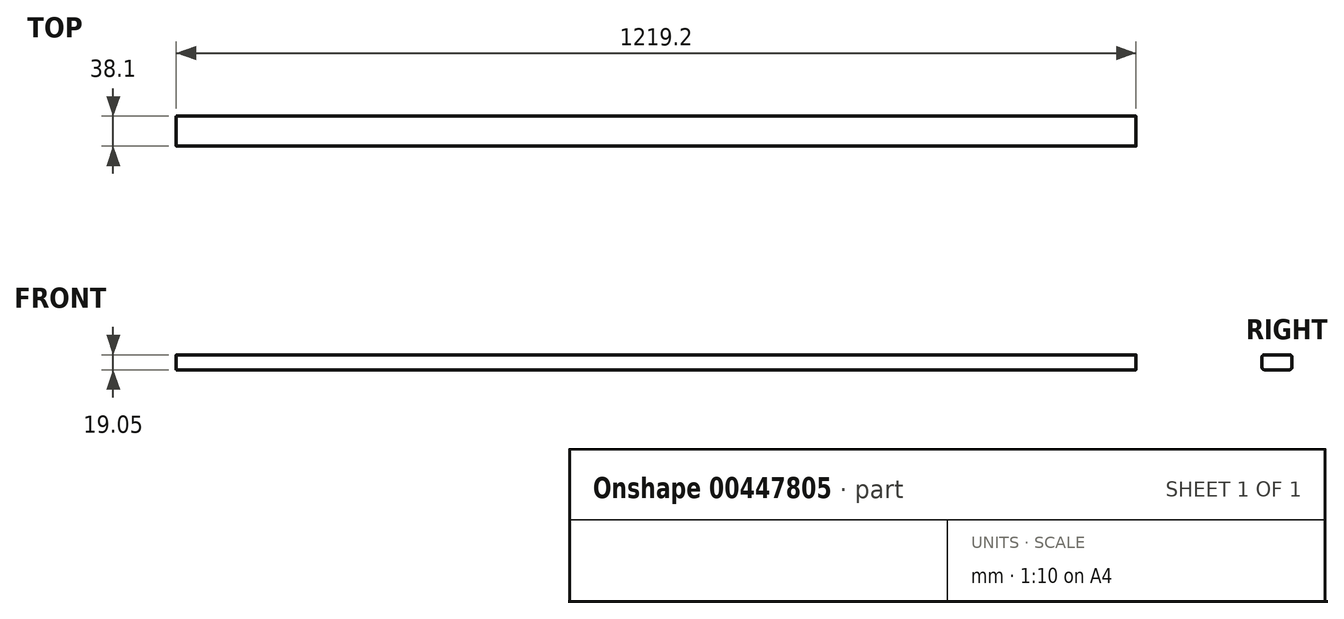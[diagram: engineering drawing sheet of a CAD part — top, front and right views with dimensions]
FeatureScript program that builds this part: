
annotation { "Feature Type Name" : "Feature", "Feature Type Description" : "" }
export const myFeature = defineFeature(function(context is Context, id is Id, definition is map)
    precondition{}
    {
        {
            var Q0;
            Q0=qCreatedBy(makeId("Right.planeOp"),FACE);
            var sketch = newSketch(context, id + "F0", { "sketchPlane" : qUnion([Q0])});
            skLineSegment(sketch, "E0.bottom", {"start": v(3.17, 0) * mm, "end": v(34.93, 0) * mm});
            skLineSegment(sketch, "E0.top", {"start": v(3.17, 19.05) * mm, "end": v(34.93, 19.05) * mm});
            skLineSegment(sketch, "E0.left", {"start": v(0, 3.18) * mm, "end": v(0, 15.88) * mm});
            skLineSegment(sketch, "E0.right", {"start": v(38.1, 3.18) * mm, "end": v(38.1, 15.88) * mm});
            skPoint(sketch, "E1.visualSharp", {"position": v(0, 19.05) * mm});
            skArc(sketch, "E1.filletArc", {"start": v(3.17, 19.05) * mm, "mid": v(0.93, 18.12) * mm, "end": v(0, 15.88) * mm});
            skPoint(sketch, "E2.visualSharp", {"position": v(0, 0) * mm});
            skArc(sketch, "E2.filletArc", {"start": v(0, 3.17) * mm, "mid": v(0.93, 0.93) * mm, "end": v(3.17, 0) * mm});
            skPoint(sketch, "E3.visualSharp", {"position": v(38.1, 19.05) * mm});
            skArc(sketch, "E3.filletArc", {"start": v(38.1, 15.88) * mm, "mid": v(37.17, 18.12) * mm, "end": v(34.93, 19.05) * mm});
            skPoint(sketch, "E4.visualSharp", {"position": v(38.1, 0) * mm});
            skArc(sketch, "E4.filletArc", {"start": v(34.93, 0) * mm, "mid": v(37.17, 0.93) * mm, "end": v(38.1, 3.18) * mm});
            skSolve(sketch);
        }
        {
            var Q0;
            Q0 = qSketchRegion(id + "F0", true);
            extrude(context, id + "F1", {"entities" : qUnion([Q0]), "depth" : 1219.2 * mm});
        }
    });
